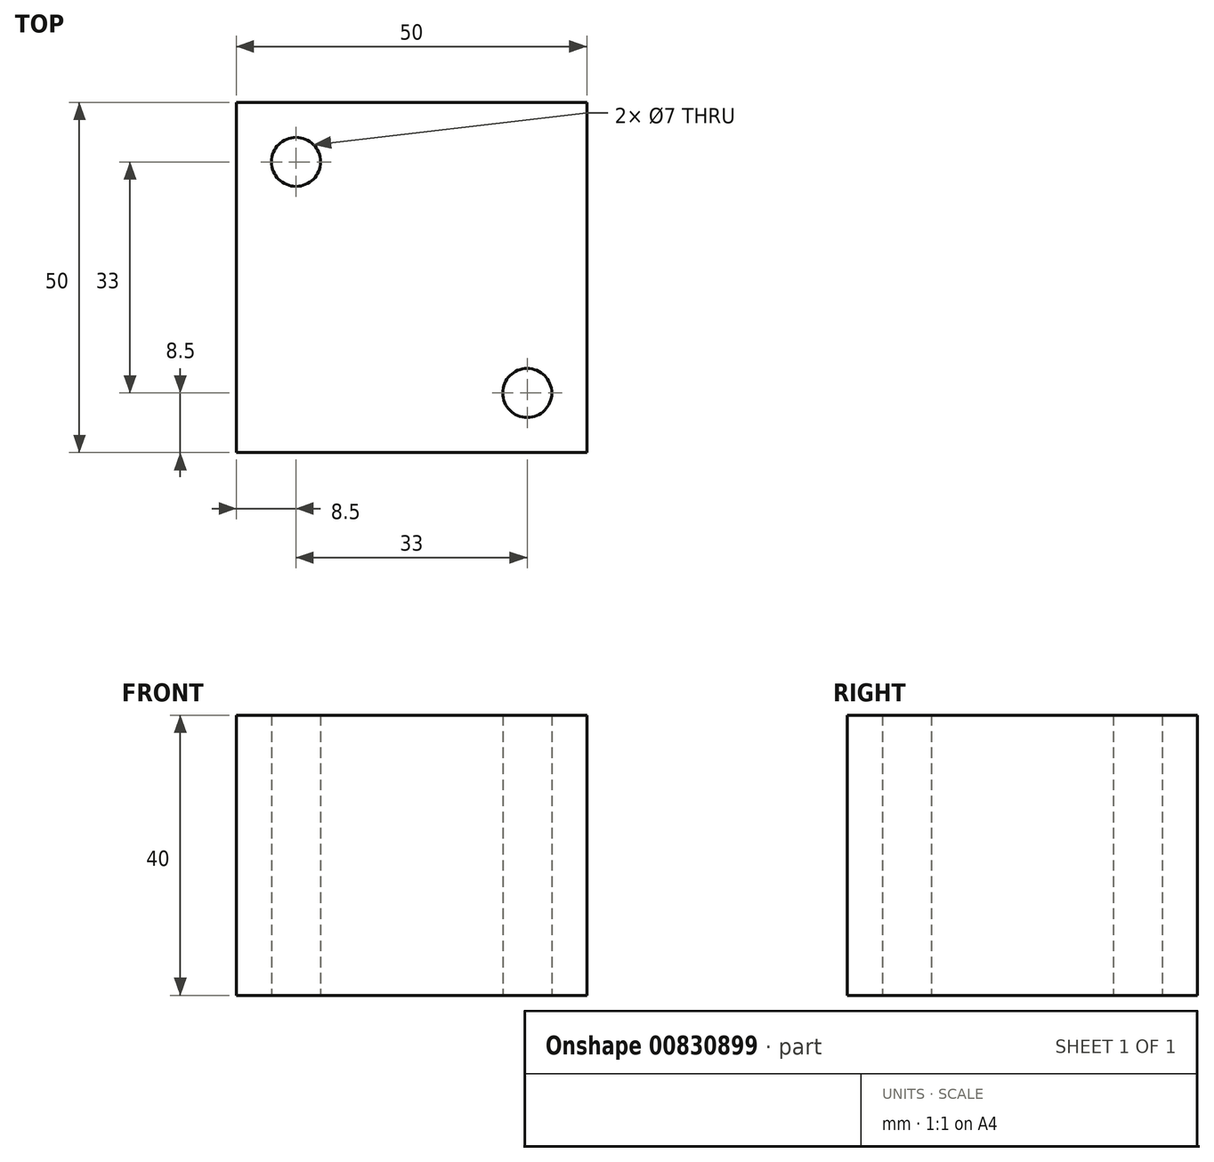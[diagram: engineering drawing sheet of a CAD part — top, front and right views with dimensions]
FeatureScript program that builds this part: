
annotation { "Feature Type Name" : "Feature", "Feature Type Description" : "" }
export const myFeature = defineFeature(function(context is Context, id is Id, definition is map)
    precondition{}
    {
        {
            var Q0;
            Q0=qCreatedBy(makeId("Top.planeOp"),FACE);
            var sketch = newSketch(context, id + "F0", { "sketchPlane" : qUnion([Q0])});
            skLineSegment(sketch, "E0.bottom", {"start": v(-25, 25) * mm, "end": v(25, 25) * mm});
            skLineSegment(sketch, "E0.top", {"start": v(-25, -25) * mm, "end": v(25, -25) * mm});
            skLineSegment(sketch, "E0.left", {"start": v(-25, 25) * mm, "end": v(-25, -25) * mm});
            skLineSegment(sketch, "E0.right", {"start": v(25, 25) * mm, "end": v(25, -25) * mm});
            skCircle(sketch, "E1", {"center": v(16.5, 16.5) * mm, "radius": 3.5 * mm});
            skCircle(sketch, "E2.MirrorC", {"center": v(16.5, -16.5) * mm, "radius": 3.5 * mm});
            skCircle(sketch, "E3.MirrorC", {"center": v(-16.5, 16.5) * mm, "radius": 3.5 * mm});
            skCircle(sketch, "E4.MirrorC", {"center": v(-16.5, -16.5) * mm, "radius": 3.5 * mm});
            skSolve(sketch);
        }
        {
            var Q0;
            Q0=makeQuery(id+"F0.imprint","IMPRINT",FACE,{"disambiguationData":[TD([[makeQuery(id+"F0.imprint","IMPRINT",EDGE,{"derivedFrom":sQuery(id+"F0.wireOp",EDGE,"E0.bottom")}),-1.0]])]});
            extrude(context, id + "F1", {"entities" : qUnion([Q0]), "depth" : 2 * mm, "offsetDistance" : 25 * mm});
        }
        {
            var Q0;
            Q0=makeQuery(id+"F0.imprint","IMPRINT",FACE,{"disambiguationData":[TD([[makeQuery(id+"F0.imprint","IMPRINT",EDGE,{"derivedFrom":sQuery(id+"F0.wireOp",EDGE,"E3.MirrorC")}),-1.0]])]});
            var Q1;
            Q1=makeQuery(id+"F0.imprint","IMPRINT",FACE,{"disambiguationData":[TD([[makeQuery(id+"F0.imprint","IMPRINT",EDGE,{"derivedFrom":sQuery(id+"F0.wireOp",EDGE,"E1")}),1.0]])]});
            var Q2;
            Q2=makeQuery(id+"F0.imprint","IMPRINT",FACE,{"disambiguationData":[TD([[makeQuery(id+"F0.imprint","IMPRINT",EDGE,{"derivedFrom":sQuery(id+"F0.wireOp",EDGE,"E2.MirrorC")}),-1.0]])]});
            var Q3;
            Q3=makeQuery(id+"F0.imprint","IMPRINT",FACE,{"disambiguationData":[TD([[makeQuery(id+"F0.imprint","IMPRINT",EDGE,{"derivedFrom":sQuery(id+"F0.wireOp",EDGE,"E4.MirrorC")}),1.0]])]});
            extrude(context, id + "F2", {"entities" : qUnion([Q0, Q1, Q2, Q3]), "operationType" : NewBodyOperationType.ADD, "depth" : 40 * mm, "offsetDistance" : 25 * mm});
        }
    });
